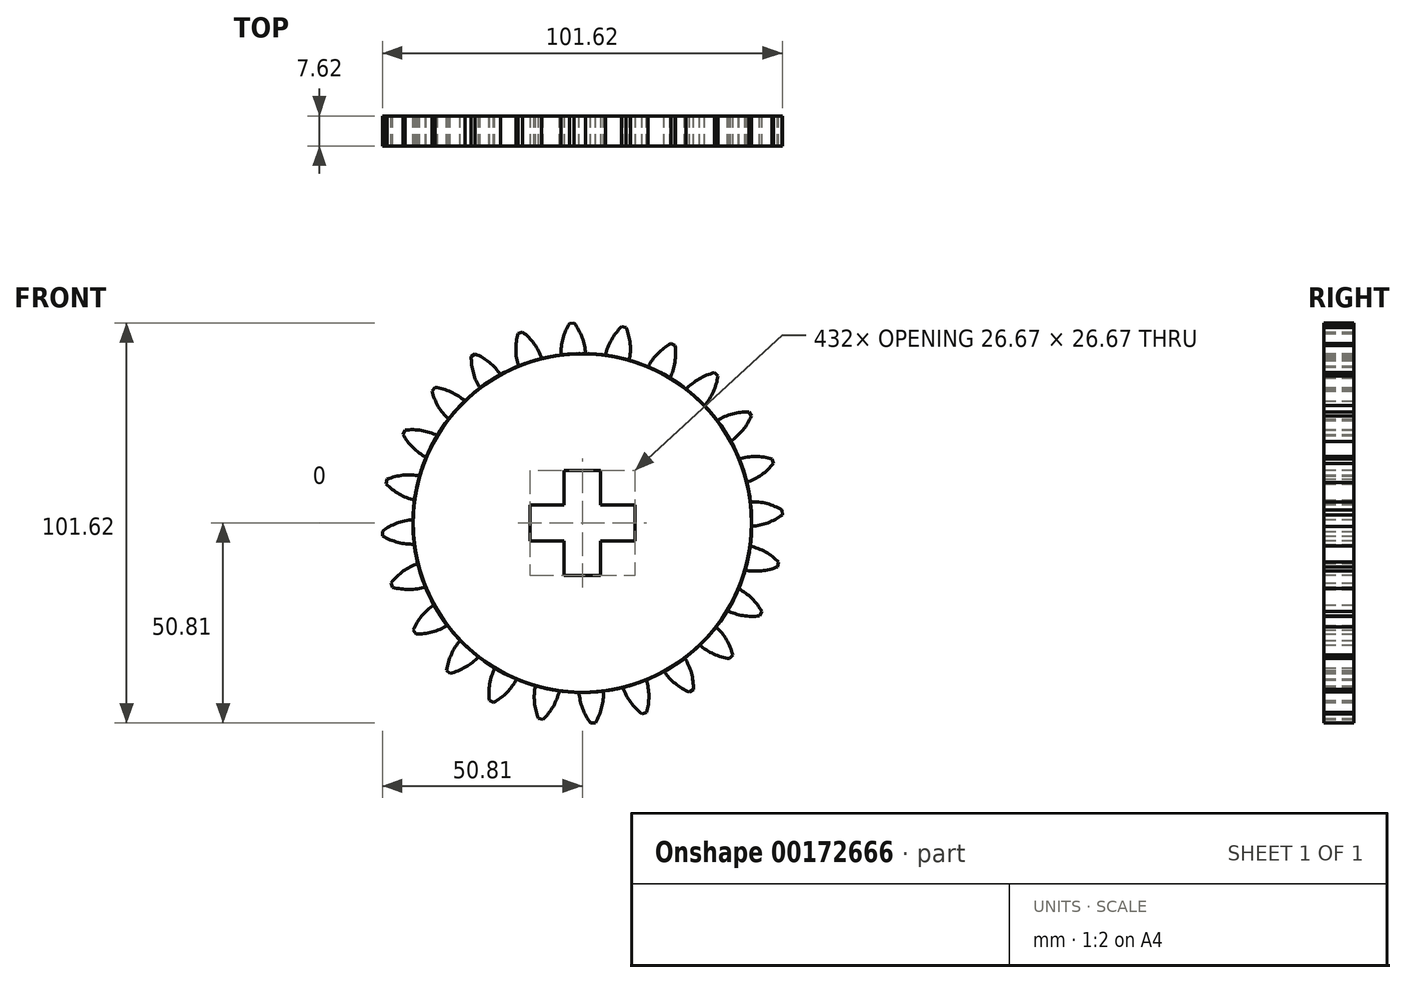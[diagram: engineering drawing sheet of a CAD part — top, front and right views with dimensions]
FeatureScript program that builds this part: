
annotation { "Feature Type Name" : "Feature", "Feature Type Description" : "" }
export const myFeature = defineFeature(function(context is Context, id is Id, definition is map)
    precondition{}
    {
        {
            var Q0;
            Q0=qCreatedBy(makeId("Front.planeOp"),FACE);
            var sketch = newSketch(context, id + "F0", { "sketchPlane" : qUnion([Q0])});
            skCircle(sketch, "E0", {"center": v(0, 0) * mm, "radius": 43.03 * mm});
            skCircle(sketch, "E1", {"center": v(0, 0) * mm, "radius": 47 * mm, "construction": true});
            skCircle(sketch, "E2", {"center": v(0, 0) * mm, "radius": 50.85 * mm, "construction": true});
            skLineSegment(sketch, "E3", {"start": v(0, 0) * mm, "end": v(0, 76.52) * mm, "construction": true});
            skLineSegment(sketch, "E4", {"start": v(0, 0) * mm, "end": v(-3.93, 74.2) * mm, "construction": true});
            skLineSegment(sketch, "E5", {"start": v(0, 47) * mm, "end": v(-39.2, 47) * mm, "construction": true});
            skLineSegment(sketch, "E6", {"start": v(0, 47) * mm, "end": v(-64.05, 23.68) * mm, "construction": true});
            skCircle(sketch, "E7", {"center": v(0, 47) * mm, "radius": 14.6 * mm, "construction": true});
            skCircle(sketch, "E8", {"center": v(0, 0) * mm, "radius": 44.16 * mm, "construction": true});
            skArc(sketch, "E9", {"start": v(-2.09, 50.8) * mm, "mid": v(-27.38, 36.82) * mm, "end": v(0.85, 43.02) * mm, "construction": true});
            skArc(sketch, "E10", {"start": v(0.85, 43.02) * mm, "mid": v(-0.05, 47.13) * mm, "end": v(-2.09, 50.8) * mm});
            skArc(sketch, "E11.MirrorCS", {"start": v(-5.39, 42.69) * mm, "mid": v(-4.92, 46.87) * mm, "end": v(-3.29, 50.74) * mm});
            skLineSegment(sketch, "E12", {"start": v(-3.29, 50.74) * mm, "end": v(-2.09, 50.8) * mm});
            skSolve(sketch);
        }
        {
            var Q0;
            Q0 = qSketchRegion(id + "F0", true);
            extrude(context, id + "F1", {"entities" : qUnion([Q0]), "endBound" : BoundingType.SYMMETRIC, "depth" : 7.62 * mm});
        }
        {
            var Q0;
            Q0=makeQuery(id+"F1.opExtrude","SWEPT_BODY",BODY,{"disambiguationData":[OSD([sQuery(id+"F0.wireOp",EDGE,"E0"),sQuery(id+"F0.wireOp",EDGE,"E10"),sQuery(id+"F0.wireOp",EDGE,"E11.MirrorCS"),sQuery(id+"F0.wireOp",EDGE,"E12")])]});
            var Q1;
            Q1=makeQuery(id+"F1.opExtrude","SWEPT_FACE",FACE,{"disambiguationData":[OSD([sQuery(id+"F0.wireOp",EDGE,"E0")])]});
            circularPattern(context, id + "F2", {"entities" : qUnion([Q0]), "axis" : qUnion([Q1]), "angle" : 15 * degree, "instanceCount" : 24});
        }
        {
            var Q0;
            Q0=makeQuery(id+"F2.opPattern","COPY",FACE,{"derivedFrom":makeQuery(id+"F1.opExtrude","CAP_FACE",FACE,{"disambiguationData":[OSD([sQuery(id+"F0.wireOp",EDGE,"E0"),sQuery(id+"F0.wireOp",EDGE,"E10"),sQuery(id+"F0.wireOp",EDGE,"E11.MirrorCS"),sQuery(id+"F0.wireOp",EDGE,"E12")])],"isStart":false}),"instanceName":"12"});
            var sketch = newSketch(context, id + "F3", { "sketchPlane" : qUnion([Q0])});
            skLineSegment(sketch, "E13.bottom", {"start": v(13.34, 4.61) * mm, "end": v(4.61, 4.61) * mm});
            skLineSegment(sketch, "E13.top", {"start": v(13.34, -4.61) * mm, "end": v(4.61, -4.61) * mm});
            skLineSegment(sketch, "E13.left", {"start": v(13.34, 4.61) * mm, "end": v(13.34, -4.61) * mm});
            skLineSegment(sketch, "E13.right", {"start": v(-13.34, 4.61) * mm, "end": v(-13.34, -4.61) * mm});
            skPoint(sketch, "E13.middle", {"position": v(0, 0) * mm});
            skLineSegment(sketch, "E14.bottom", {"start": v(-4.61, 13.33) * mm, "end": v(4.61, 13.34) * mm});
            skLineSegment(sketch, "E14.top", {"start": v(-4.61, -13.34) * mm, "end": v(4.61, -13.33) * mm});
            skLineSegment(sketch, "E14.left", {"start": v(-4.61, 13.33) * mm, "end": v(-4.61, 4.61) * mm});
            skLineSegment(sketch, "E14.right", {"start": v(4.61, 13.34) * mm, "end": v(4.61, 4.61) * mm});
            skLineSegment(sketch, "E15.trimOffspring", {"start": v(-4.61, 4.61) * mm, "end": v(-13.34, 4.61) * mm});
            skLineSegment(sketch, "E16.trimOffspring", {"start": v(4.61, -4.61) * mm, "end": v(4.61, -13.33) * mm});
            skLineSegment(sketch, "E17.trimOffspring", {"start": v(-4.61, -4.61) * mm, "end": v(-13.34, -4.61) * mm});
            skLineSegment(sketch, "E18.trimOffspring", {"start": v(-4.61, -4.61) * mm, "end": v(-4.61, -13.34) * mm});
            skSolve(sketch);
        }
        {
            var Q0;
            Q0=makeQuery(id+"F3.imprint","IMPRINT",FACE,{"disambiguationData":[TD([[makeQuery(id+"F3.imprint","IMPRINT",EDGE,{"derivedFrom":sQuery(id+"F3.wireOp",EDGE,"E13.bottom")}),1.0]])]});
            extrude(context, id + "F4", {"entities" : qUnion([Q0]), "operationType" : NewBodyOperationType.REMOVE, "endBound" : BoundingType.THROUGH_ALL, "oppositeDirection" : true, "depth" : 25.4 * mm});
        }
    });
